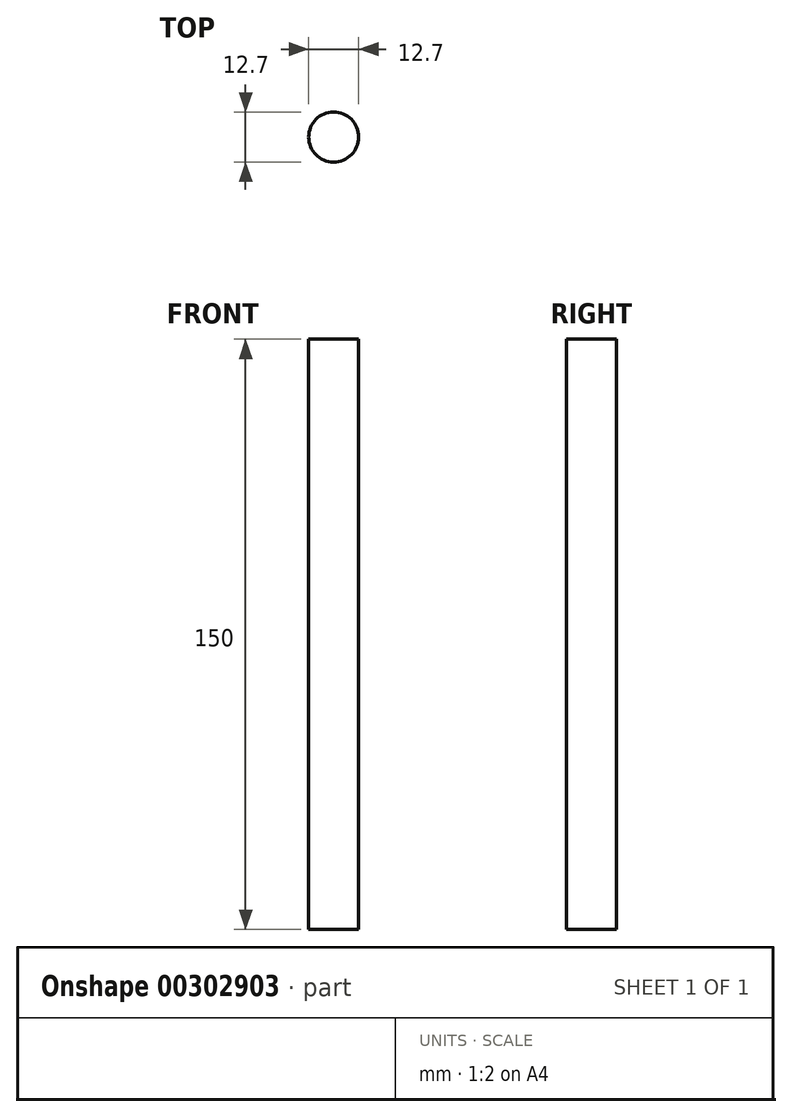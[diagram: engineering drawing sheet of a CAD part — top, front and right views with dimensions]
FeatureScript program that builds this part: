
annotation { "Feature Type Name" : "Feature", "Feature Type Description" : "" }
export const myFeature = defineFeature(function(context is Context, id is Id, definition is map)
    precondition{}
    {
        {
            var Q0;
            Q0=qCreatedBy(makeId("Top.planeOp"),FACE);
            var sketch = newSketch(context, id + "F0", { "sketchPlane" : qUnion([Q0])});
            skCircle(sketch, "E0", {"center": v(0, 0) * mm, "radius": 6.35 * mm});
            skSolve(sketch);
        }
        {
            var Q0;
            Q0 = qSketchRegion(id + "F0", true);
            extrude(context, id + "F1", {"entities" : qUnion([Q0]), "depth" : 150 * mm});
        }
    });
